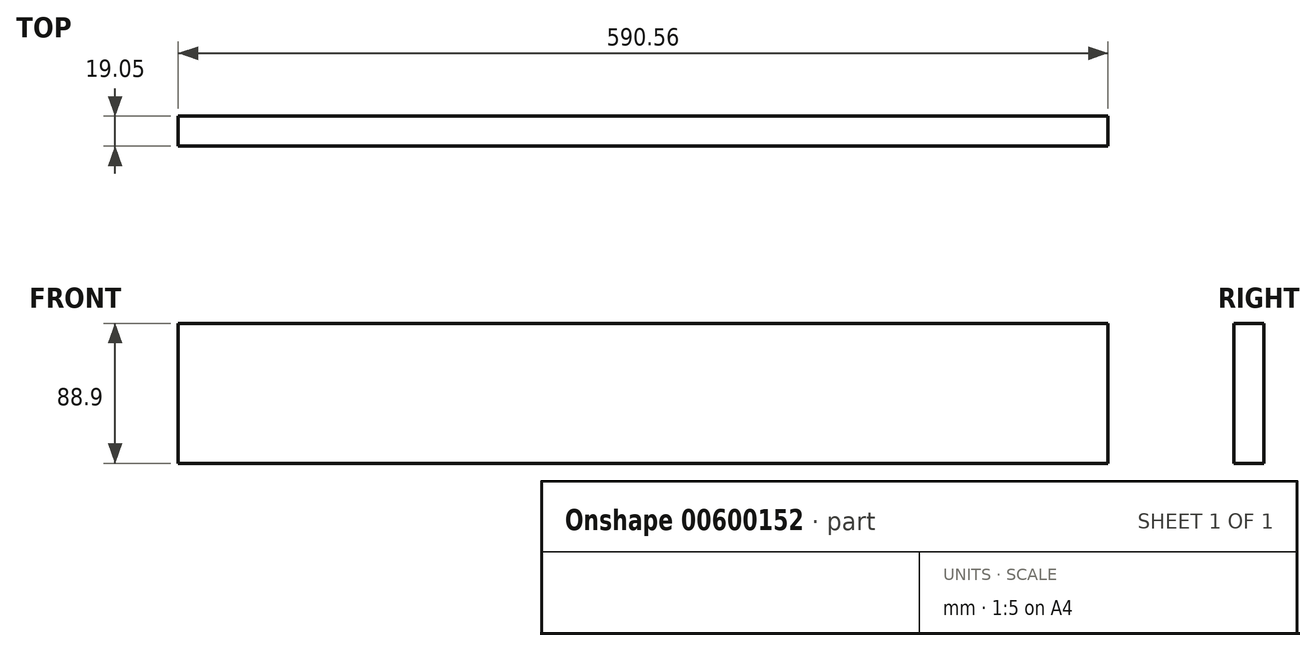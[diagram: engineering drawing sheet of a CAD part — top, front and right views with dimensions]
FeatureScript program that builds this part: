
annotation { "Feature Type Name" : "Feature", "Feature Type Description" : "" }
export const myFeature = defineFeature(function(context is Context, id is Id, definition is map)
    precondition{}
    {
        {
            var Q0;
            Q0=qCreatedBy(makeId("Front.planeOp"),FACE);
            var sketch = newSketch(context, id + "F0", { "sketchPlane" : qUnion([Q0])});
            skLineSegment(sketch, "E0.bottom", {"start": v(-295.28, 44.45) * mm, "end": v(295.28, 44.45) * mm});
            skLineSegment(sketch, "E0.top", {"start": v(-295.28, -44.45) * mm, "end": v(295.28, -44.45) * mm});
            skLineSegment(sketch, "E0.left", {"start": v(-295.28, 44.45) * mm, "end": v(-295.28, -44.45) * mm});
            skLineSegment(sketch, "E0.right", {"start": v(295.28, 44.45) * mm, "end": v(295.28, -44.45) * mm});
            skLineSegment(sketch, "E1", {"start": v(-295.28, -44.45) * mm, "end": v(295.28, 44.45) * mm, "construction": true});
            skSolve(sketch);
        }
        {
            var Q0;
            Q0 = qSketchRegion(id + "F0", true);
            extrude(context, id + "F1", {"entities" : qUnion([Q0]), "depth" : 19.05 * mm, "offsetDistance" : 25.4 * mm});
        }
    });
